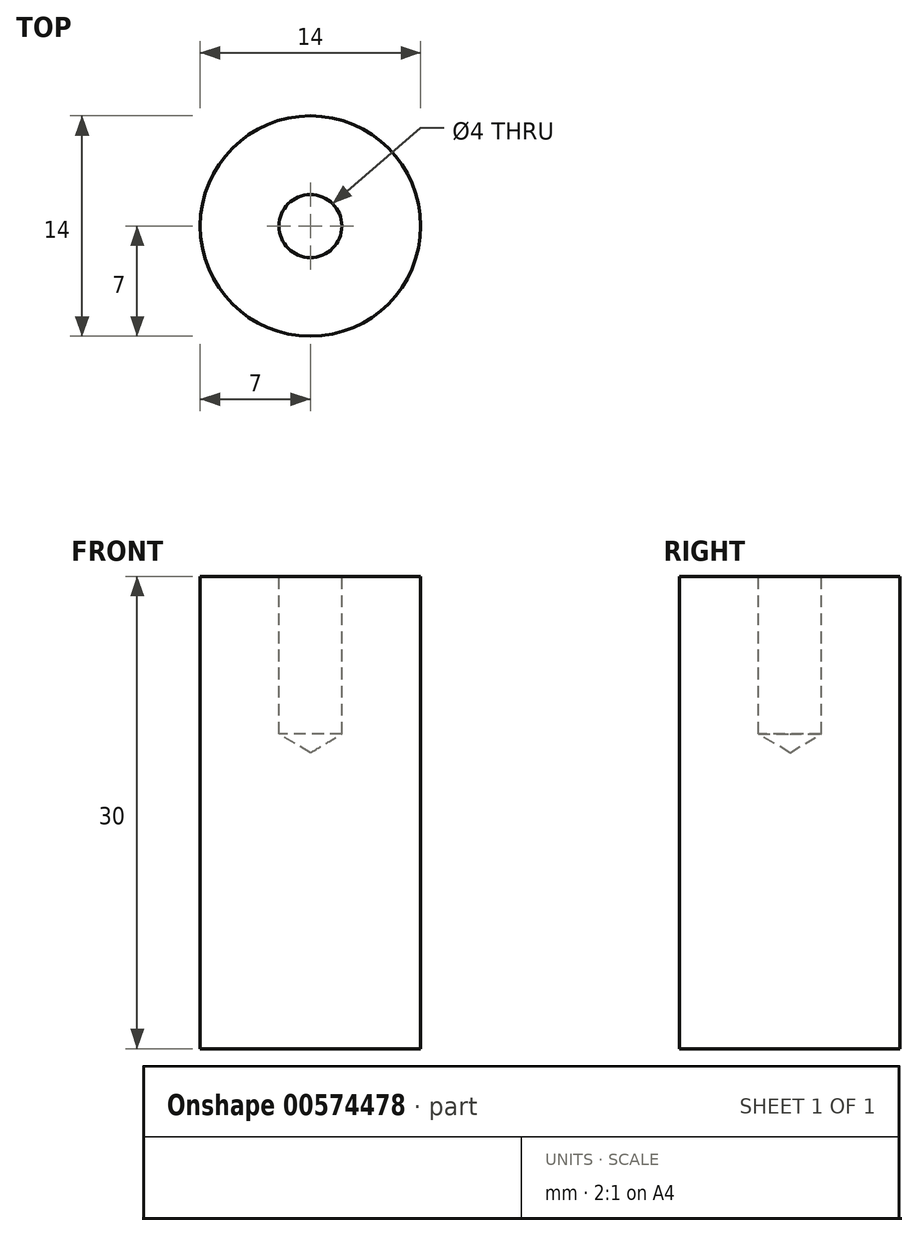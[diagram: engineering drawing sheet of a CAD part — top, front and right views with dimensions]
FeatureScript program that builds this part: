
annotation { "Feature Type Name" : "Feature", "Feature Type Description" : "" }
export const myFeature = defineFeature(function(context is Context, id is Id, definition is map)
    precondition{}
    {
        {
            var Q0;
            Q0=qCreatedBy(makeId("Top.planeOp"),FACE);
            var sketch = newSketch(context, id + "F0", { "sketchPlane" : qUnion([Q0])});
            skCircle(sketch, "E0", {"center": v(0, 0) * mm, "radius": 7 * mm});
            skSolve(sketch);
        }
        {
            var Q0;
            Q0=makeQuery(id+"F0.imprint","IMPRINT",FACE,{"disambiguationData":[TD([[makeQuery(id+"F0.imprint","IMPRINT",EDGE,{"derivedFrom":sQuery(id+"F0.wireOp",EDGE,"E0")}),1.0]])]});
            extrude(context, id + "F1", {"entities" : qUnion([Q0]), "depth" : 30 * mm, "offsetDistance" : 25 * mm});
        }
        {
            var Q0;
            Q0=makeQuery(id+"F1.opExtrude","CAP_FACE",FACE,{"disambiguationData":[OSD([sQuery(id+"F0.wireOp",EDGE,"E0")])],"isStart":false});
            var sketch = newSketch(context, id + "F2", { "sketchPlane" : qUnion([Q0])});
            skPoint(sketch, "E1", {"position": v(0, 0) * mm});
            skSolve(sketch);
        }
        {
            var Q0;
            Q0=sQuery(id+"F2.wireOp",VERTEX,"E1");
            var Q1;
            Q1=makeQuery(id+"F1.opExtrude","SWEPT_BODY",BODY,{"disambiguationData":[OSD([sQuery(id+"F0.wireOp",EDGE,"E0")])]});
            hole(context, id + "F3", {"style" : HoleStyle.SIMPLE, "endStyle" : HoleEndStyle.BLIND, "holeDiameter" : 4 * mm, "holeDepth" : 10 * mm, "isTappedThrough" : true, "tappedDepth" : 12 * mm, "tapClearance" : 3, "locations" : qUnion([Q0]), "scope" : qUnion([Q1])});
        }
    });
